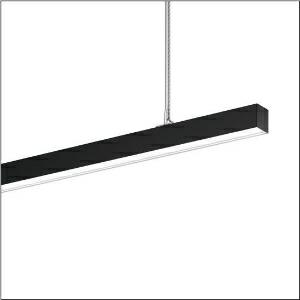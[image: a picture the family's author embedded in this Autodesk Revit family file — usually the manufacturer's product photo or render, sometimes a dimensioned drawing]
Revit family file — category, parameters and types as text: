
# Revit family: silica_21_51mx30db35bb
name_source: partatom
category: Lighting Fixtures
units: mm (PartAtom-declared; Revit-internal decimal feet)

## family parameters
Cut with Voids When Loaded = No
Host = Face
Light Source = No
Part Type = Normal
Room Calculation Point = No
Round Connector Dimension = Use Diameter
Shared = No

## types (1)
- --- (1 x LED, 5260 lm, 34.1 W, 3000K)
    Apparent Load = 34 VA
    CIE Flux Codes = 47 79 96 57 100
    Color Rendering = 80
    Color Temperature = 3000K
    Default Elevation = 1800 mm
    Description = Silica 21, office luminaire, primary optical cover: cover, of PMMA, opal, light emission: direct/indirect distribution, primary light characteristic: symmetric, installation type: suspended mounting, LED, rated luminous flux: 5.260lm, luminous efficacy: 154lm/W, light colour: 830, colour temperature: 3000K, control gear: DALI 2, with terminal, 3+2-pole, max. 2.5mm², mains connection: 220..240V, AC, 50/60Hz, rated input power: 34.1W, luminaire housing, of aluminium, matt jet black (RAL 9005), length: 1.504mm, width: 53mm, height: 53mm, protection rating (complete): IP20, insulation class (complete): insulation class I (protective earthing), certification: CE, permissible operating ambient temperature: 0..+35°C, standard: EN 50419, packaging unit: 1 piece
    Height = 53 mm
    Lamp = 1 x LED
    Lamp Light Flux = 5260 lm
    Lamp Power = 34.1 W
    Lamp count = 1
    Length = 1504 mm
    Luminous efficacy = 154 lm/W
    Manufacturer = Siteco
    ModVariant = No
    Model = 51MX30DB35BB
    Mounting Place = Ceiling
    Mounting Type = Pendant
    Number of Poles = 1
    OnlyDefault = Yes
    Power Factor = 1
    Product Name = Silica 21
    Product group = office luminaire | ceiling pendant
    ProductGroupID = 903
    Protection Class = Protection class I
    Protection Degree = IP 20
    RLX_Detail_Level = 1
    RLX_Emergency_Light_Flux = 0 lm
    RLX_Emergency_Type = 0
    RLX_Emergency_Type_DB = No
    RlxData = <blob elided: 26057 chars, md5=6abca75d>
    Socket = socket
    Standby Power = 0 W
    System Light Flux = 5260 lm
    System Power = 34 W
    Type Comments = factory setting: luminous flux: 100 % | dim-lin: 254 | 233 mA
    Type Image = l_1335856.jpg
    URL = http://relux.com
    VarID = @adj_117145
    Voltage = 0 V
    Weight = 0.00 kg
    Width = 53 mm

## geometry (parser evidence)
native form markers: Blend x4, Sweep x12
no freeform markers — native parametric forms only
